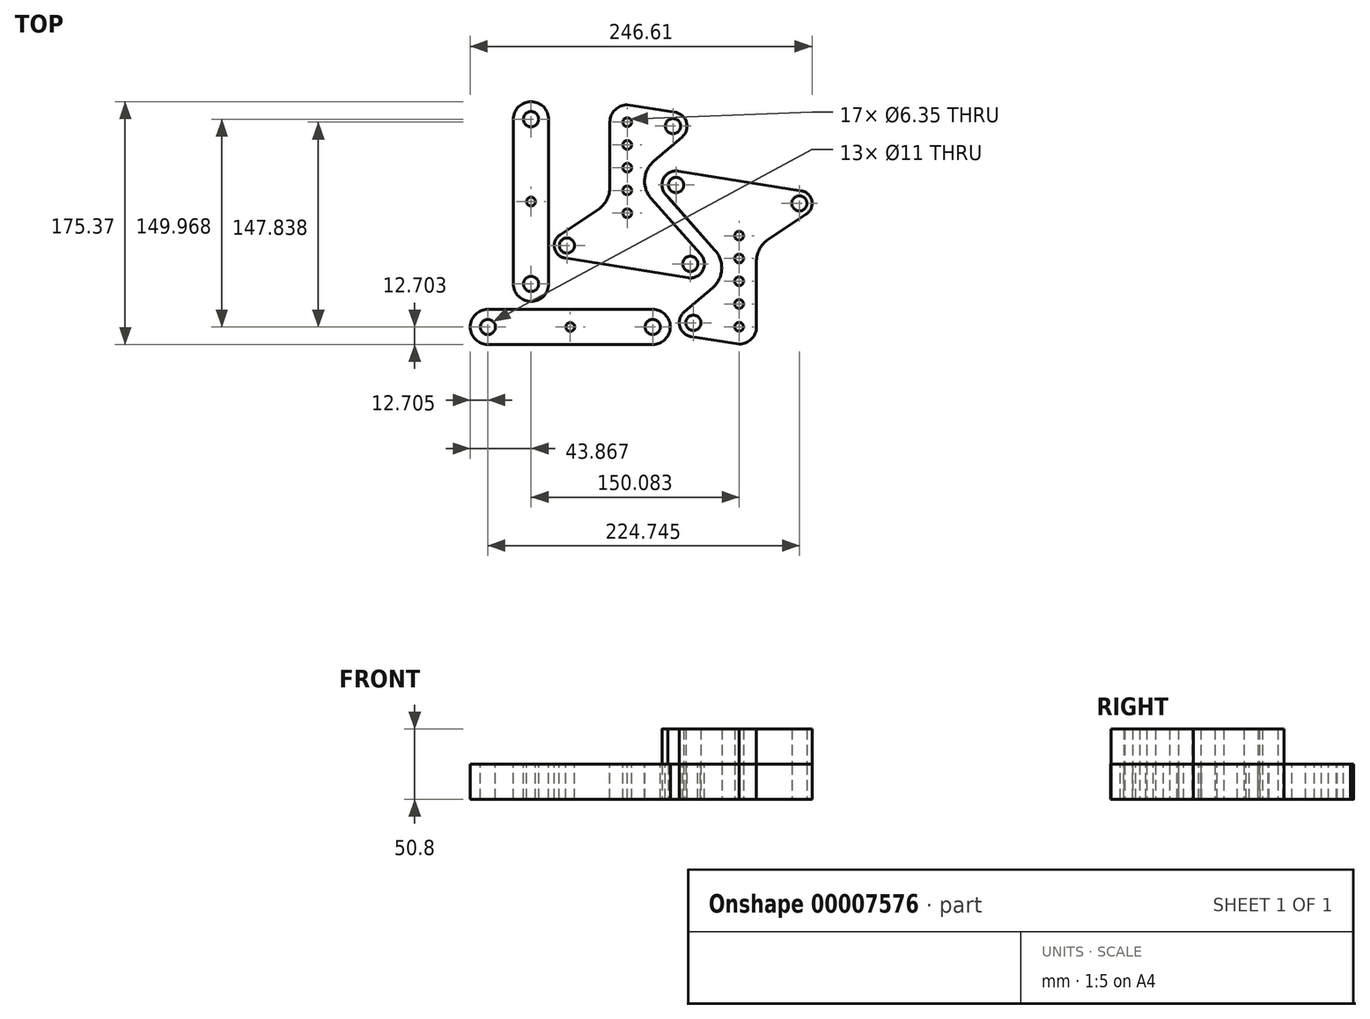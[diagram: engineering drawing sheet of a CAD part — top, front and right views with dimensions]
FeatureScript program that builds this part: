
annotation { "Feature Type Name" : "Feature", "Feature Type Description" : "" }
export const myFeature = defineFeature(function(context is Context, id is Id, definition is map)
    precondition{}
    {
        {
            var Q0;
            Q0=qCreatedBy(makeId("Top.planeOp"),FACE);
            var sketch = newSketch(context, id + "F0", { "sketchPlane" : qUnion([Q0])});
            skLineSegment(sketch, "E0", {"start": v(-216.15, 34.82) * mm, "end": v(113.5, 34.82) * mm});
            skLineSegment(sketch, "E1", {"start": v(-210.76, 13.28) * mm, "end": v(113.5, 13.28) * mm});
            skLineSegment(sketch, "E2", {"start": v(113.5, 0) * mm, "end": v(-200.85, 0) * mm});
            skLineSegment(sketch, "E3", {"start": v(-198.6, -86.18) * mm, "end": v(113.5, -86.18) * mm});
            skLineSegment(sketch, "E4", {"start": v(113.5, 34.82) * mm, "end": v(113.5, -86.18) * mm});
            skLineSegment(sketch, "E5", {"start": v(0, 62.68) * mm, "end": v(0, -125.74) * mm});
            skPoint(sketch, "E6", {"position": v(-45.5, 13.28) * mm});
            skPoint(sketch, "E7", {"position": v(43.5, 0) * mm});
            skPoint(sketch, "E8", {"position": v(-33, -86.18) * mm});
            skSolve(sketch);
        }
        {
            var Q0;
            Q0=qCreatedBy(makeId("Top.planeOp"),FACE);
            var sketch = newSketch(context, id + "F1", { "sketchPlane" : qUnion([Q0])});
            skLineSegment(sketch, "E9", {"start": v(113.5, 34.82) * mm, "end": v(113.5, -455.58) * mm});
            skLineSegment(sketch, "E10", {"start": v(113.5, 34.82) * mm, "end": v(-885.82, 34.82) * mm});
            skLineSegment(sketch, "E11", {"start": v(113.5, -7.25) * mm, "end": v(-888.28, -7.25) * mm});
            skLineSegment(sketch, "E12", {"start": v(113.5, -81.11) * mm, "end": v(-225.14, -81.11) * mm});
            skLineSegment(sketch, "E13", {"start": v(113.5, -46.44) * mm, "end": v(-202.6, -46.44) * mm});
            skLineSegment(sketch, "E14", {"start": v(113.5, -41.92) * mm, "end": v(-189.33, -41.92) * mm});
            skPoint(sketch, "E15", {"position": v(105.43, -46.44) * mm});
            skPoint(sketch, "E16", {"position": v(70.76, -7.25) * mm});
            skPoint(sketch, "E17", {"position": v(-31.57, -46.44) * mm});
            skPoint(sketch, "E18", {"position": v(31.57, -41.92) * mm});
            skPoint(sketch, "E19", {"position": v(-105.43, -41.92) * mm});
            skPoint(sketch, "E20", {"position": v(-66.24, -7.25) * mm});
            skPoint(sketch, "E21", {"position": v(66.24, -81.11) * mm});
            skPoint(sketch, "E22", {"position": v(-70.76, -81.11) * mm});
            skSolve(sketch);
        }
        {
            var Q0;
            Q0=qCreatedBy(makeId("Top.planeOp"),FACE);
            var sketch = newSketch(context, id + "F2", { "sketchPlane" : qUnion([Q0])});
            skCircle(sketch, "E23", {"center": v(-66.24, -7.25) * mm, "radius": 19.05 * mm});
            skCircle(sketch, "E24", {"center": v(-105.43, -41.92) * mm, "radius": 19.05 * mm});
            skCircle(sketch, "E25", {"center": v(-31.57, -46.44) * mm, "radius": 19.05 * mm});
            skCircle(sketch, "E26", {"center": v(-70.76, -81.11) * mm, "radius": 19.05 * mm});
            skCircle(sketch, "E27", {"center": v(70.76, -7.25) * mm, "radius": 19.05 * mm});
            skCircle(sketch, "E28", {"center": v(31.57, -41.92) * mm, "radius": 19.05 * mm});
            skCircle(sketch, "E29", {"center": v(105.43, -46.44) * mm, "radius": 19.05 * mm});
            skCircle(sketch, "E30", {"center": v(66.24, -81.11) * mm, "radius": 19.05 * mm});
            skCircle(sketch, "E31", {"center": v(43.5, 0) * mm, "radius": 9.16 * mm});
            skCircle(sketch, "E32", {"center": v(-45.5, 13.28) * mm, "radius": 10.13 * mm});
            skCircle(sketch, "E33", {"center": v(-45.5, 13.28) * mm, "radius": 5.5 * mm});
            skCircle(sketch, "E34", {"center": v(43.5, 0) * mm, "radius": 5.5 * mm});
            skCircle(sketch, "E35", {"center": v(-33, -86.18) * mm, "radius": 5.5 * mm});
            skCircle(sketch, "E36", {"center": v(-33, -86.18) * mm, "radius": 10.13 * mm});
            skLineSegment(sketch, "E37", {"start": v(-43.9, 23.28) * mm, "end": v(44.95, 9.04) * mm});
            skLineSegment(sketch, "E38", {"start": v(48.6, -7.61) * mm, "end": v(20.98, -26.09) * mm});
            skLineSegment(sketch, "E39", {"start": v(-53.08, 6.56) * mm, "end": v(-17.31, -33.8) * mm});
            skCircle(sketch, "E40", {"center": v(0, -89.06) * mm, "radius": 12.52 * mm});
            skLineSegment(sketch, "E41", {"start": v(-34.56, -96.2) * mm, "end": v(0, -101.58) * mm});
            skLineSegment(sketch, "E42", {"start": v(12.52, -89.06) * mm, "end": v(12.52, -42.2) * mm});
            skLineSegment(sketch, "E43", {"start": v(-39.61, -78.5) * mm, "end": v(-19.14, -60.88) * mm});
            skPoint(sketch, "E44", {"position": v(0, -23.32) * mm});
            skCircle(sketch, "E45", {"center": v(0, -23.32) * mm, "radius": 3.18 * mm});
            skCircle(sketch, "E46", {"center": v(0, -39.75) * mm, "radius": 3.18 * mm});
            skCircle(sketch, "E47", {"center": v(0, -56.19) * mm, "radius": 3.18 * mm});
            skCircle(sketch, "E48", {"center": v(0, -72.62) * mm, "radius": 3.18 * mm});
            skCircle(sketch, "E49", {"center": v(0, -89.06) * mm, "radius": 3.18 * mm});
            skLineSegment(sketch, "E50", {"start": v(0, -101.58) * mm, "end": v(0, 16.25) * mm});
            skSolve(sketch);
        }
        {
            var Q0;
            {var subQ13=sQuery(id+"F2.wireOp",EDGE,"E43");Q0=makeQuery(id+"F2.imprint","IMPRINT",FACE,{"disambiguationData":[TD([[makeQuery(id+"F2.imprint","IMPRINT",EDGE,{"derivedFrom":subQ13}),-1.0]])]});}
            var Q1;
            {var subQ18=sQuery(id+"F2.wireOp",EDGE,"E38");Q1=makeQuery(id+"F2.imprint","IMPRINT",FACE,{"disambiguationData":[TD([[makeQuery(id+"F2.imprint","IMPRINT",EDGE,{"derivedFrom":subQ18}),-1.0]])]});}
            var Q2;
            Q2=makeQuery(id+"F2.imprint","IMPRINT",FACE,{"disambiguationData":[TD([[makeQuery(id+"F2.imprint","IMPRINT",EDGE,{"derivedFrom":sQuery(id+"F2.wireOp",EDGE,"E33")}),-1.0]])]});
            var Q3;
            Q3=makeQuery(id+"F2.imprint","IMPRINT",FACE,{"disambiguationData":[TD([[makeQuery(id+"F2.imprint","IMPRINT",EDGE,{"derivedFrom":sQuery(id+"F2.wireOp",EDGE,"E34")}),-1.0]])]});
            var Q4;
            {var subQ3=sQuery(id+"F2.wireOp",EDGE,"E40");var subQ7=makeQuery(id+"F2.imprint","INTERSECT",VERTEX,{"derivedFrom":[subQ3,sQuery(id+"F2.wireOp",EDGE,"E42")]});Q4=makeQuery(id+"F2.imprint","IMPRINT",FACE,{"disambiguationData":[TD([[makeQuery(id+"F2.imprint","IMPRINT",EDGE,{"disambiguationData":[TD([[subQ7,-1.0]])],"derivedFrom":subQ3}),1.0]])]});}
            var Q5;
            {var subQ3=sQuery(id+"F2.wireOp",EDGE,"E40");var subQ6=sQuery(id+"F2.wireOp",EDGE,"E41");var subQ8=makeQuery(id+"F2.imprint","INTERSECT",VERTEX,{"derivedFrom":[subQ3,subQ6]});Q5=makeQuery(id+"F2.imprint","IMPRINT",FACE,{"disambiguationData":[TD([[makeQuery(id+"F2.imprint","IMPRINT",EDGE,{"disambiguationData":[TD([[subQ8,1.0]])],"derivedFrom":subQ3}),1.0]])]});}
            var Q6;
            Q6=makeQuery(id+"F2.imprint","IMPRINT",FACE,{"disambiguationData":[TD([[makeQuery(id+"F2.imprint","IMPRINT",EDGE,{"derivedFrom":sQuery(id+"F2.wireOp",EDGE,"E35")}),-1.0]])]});
            extrude(context, id + "F3", {"entities" : qUnion([Q0, Q1, Q2, Q3, Q4, Q5, Q6]), "depth" : 25.4 * mm});
        }
        {
            var Q0;
            Q0=makeQuery(id+"F3.opExtrude","CAP_FACE",FACE,{"disambiguationData":[OSD([sQuery(id+"F2.wireOp",EDGE,"E23"),sQuery(id+"F2.wireOp",EDGE,"E25"),sQuery(id+"F2.wireOp",EDGE,"E28"),sQuery(id+"F2.wireOp",EDGE,"E31"),sQuery(id+"F2.wireOp",EDGE,"E32"),sQuery(id+"F2.wireOp",EDGE,"E33"),sQuery(id+"F2.wireOp",EDGE,"E34"),sQuery(id+"F2.wireOp",EDGE,"E35"),sQuery(id+"F2.wireOp",EDGE,"E36"),sQuery(id+"F2.wireOp",EDGE,"E37"),sQuery(id+"F2.wireOp",EDGE,"E38"),sQuery(id+"F2.wireOp",EDGE,"E39"),sQuery(id+"F2.wireOp",EDGE,"E40"),sQuery(id+"F2.wireOp",EDGE,"E41"),sQuery(id+"F2.wireOp",EDGE,"E42"),sQuery(id+"F2.wireOp",EDGE,"E43"),sQuery(id+"F2.wireOp",EDGE,"E45"),sQuery(id+"F2.wireOp",EDGE,"E46"),sQuery(id+"F2.wireOp",EDGE,"E47"),sQuery(id+"F2.wireOp",EDGE,"E48"),sQuery(id+"F2.wireOp",EDGE,"E49")])],"isStart":false});
            var sketch = newSketch(context, id + "F4", { "sketchPlane" : qUnion([Q0])});
            skArc(sketch, "E51", {"start": v(-39.61, -78.5) * mm, "mid": v(-42.74, -88.96) * mm, "end": v(-34.56, -96.2) * mm});
            skArc(sketch, "E52", {"start": v(48.6, -7.61) * mm, "mid": v(52.45, 1.96) * mm, "end": v(44.95, 9.04) * mm});
            skArc(sketch, "E53", {"start": v(20.98, -26.09) * mm, "mid": v(14.7, -33.07) * mm, "end": v(12.52, -42.2) * mm});
            skArc(sketch, "E54", {"start": v(0, -101.58) * mm, "mid": v(8.85, -97.91) * mm, "end": v(12.52, -89.06) * mm});
            skArc(sketch, "E55", {"start": v(-19.14, -60.88) * mm, "mid": v(-12.56, -47.72) * mm, "end": v(-17.31, -33.8) * mm});
            skArc(sketch, "E56", {"start": v(-43.9, 23.28) * mm, "mid": v(-54.51, 17.91) * mm, "end": v(-52.7, 6.15) * mm});
            skLineSegment(sketch, "E57", {"start": v(-17.31, -33.8) * mm, "end": v(-52.7, 6.15) * mm});
            skLineSegment(sketch, "E58", {"start": v(-43.9, 23.28) * mm, "end": v(44.95, 9.04) * mm});
            skLineSegment(sketch, "E59", {"start": v(48.6, -7.61) * mm, "end": v(20.98, -26.09) * mm});
            skLineSegment(sketch, "E60", {"start": v(12.52, -42.2) * mm, "end": v(12.52, -89.06) * mm});
            skLineSegment(sketch, "E61", {"start": v(0, -101.58) * mm, "end": v(-34.56, -96.2) * mm});
            skLineSegment(sketch, "E62", {"start": v(-39.61, -78.5) * mm, "end": v(-19.14, -60.88) * mm});
            skCircle(sketch, "E63", {"center": v(-33, -86.18) * mm, "radius": 5.5 * mm});
            skCircle(sketch, "E64", {"center": v(0, -89.06) * mm, "radius": 3.18 * mm});
            skCircle(sketch, "E65", {"center": v(0, -72.62) * mm, "radius": 3.18 * mm});
            skCircle(sketch, "E66", {"center": v(-45.5, 13.28) * mm, "radius": 5.5 * mm});
            skCircle(sketch, "E67", {"center": v(43.5, 0) * mm, "radius": 5.5 * mm});
            skCircle(sketch, "E68", {"center": v(0, -56.19) * mm, "radius": 3.18 * mm});
            skCircle(sketch, "E69", {"center": v(0, -39.75) * mm, "radius": 3.18 * mm});
            skCircle(sketch, "E70", {"center": v(0, -23.32) * mm, "radius": 3.18 * mm});
            skLineSegment(sketch, "E71", {"start": v(-162.78, 60.77) * mm, "end": v(-162.78, -58.13) * mm});
            skLineSegment(sketch, "E72", {"start": v(-137.38, -58.13) * mm, "end": v(-137.38, 60.77) * mm});
            skArc(sketch, "E73", {"start": v(-137.38, 60.77) * mm, "mid": v(-150.08, 73.47) * mm, "end": v(-162.78, 60.77) * mm});
            skArc(sketch, "E74", {"start": v(-162.78, -58.13) * mm, "mid": v(-150.08, -70.83) * mm, "end": v(-137.38, -58.13) * mm});
            skCircle(sketch, "E75", {"center": v(-150.08, 60.77) * mm, "radius": 5.5 * mm});
            skCircle(sketch, "E76", {"center": v(-150.08, -58.13) * mm, "radius": 5.5 * mm});
            skCircle(sketch, "E77", {"center": v(-150.08, 1.32) * mm, "radius": 3.18 * mm});
            skPoint(sketch, "E77.centerSnap0", {"position": v(-121.63, -106.83) * mm});
            skArc(sketch, "E78", {"start": v(-41.09, 48.09) * mm, "mid": v(-37.96, 58.55) * mm, "end": v(-46.14, 65.78) * mm});
            skArc(sketch, "E79", {"start": v(-129.3, -22.8) * mm, "mid": v(-133.15, -32.37) * mm, "end": v(-125.65, -39.46) * mm});
            skArc(sketch, "E80", {"start": v(-101.68, -4.33) * mm, "mid": v(-95.4, 2.66) * mm, "end": v(-93.22, 11.8) * mm});
            skArc(sketch, "E81", {"start": v(-80.7, 71.16) * mm, "mid": v(-89.55, 67.5) * mm, "end": v(-93.22, 58.64) * mm});
            skArc(sketch, "E82", {"start": v(-61.56, 30.46) * mm, "mid": v(-68.14, 17.3) * mm, "end": v(-63.39, 3.4) * mm});
            skArc(sketch, "E83", {"start": v(-36.8, -53.7) * mm, "mid": v(-26.19, -48.33) * mm, "end": v(-28, -36.57) * mm});
            skLineSegment(sketch, "E84", {"start": v(-63.39, 3.4) * mm, "end": v(-28, -36.57) * mm});
            skLineSegment(sketch, "E85", {"start": v(-36.8, -53.7) * mm, "end": v(-125.65, -39.46) * mm});
            skLineSegment(sketch, "E86", {"start": v(-129.3, -22.8) * mm, "end": v(-101.68, -4.33) * mm});
            skLineSegment(sketch, "E87", {"start": v(-93.22, 11.8) * mm, "end": v(-93.22, 58.64) * mm});
            skLineSegment(sketch, "E88", {"start": v(-80.7, 71.16) * mm, "end": v(-46.14, 65.78) * mm});
            skLineSegment(sketch, "E89", {"start": v(-41.09, 48.09) * mm, "end": v(-61.56, 30.46) * mm});
            skCircle(sketch, "E90", {"center": v(-47.7, 55.77) * mm, "radius": 5.5 * mm});
            skCircle(sketch, "E91", {"center": v(-80.7, 58.64) * mm, "radius": 3.18 * mm});
            skCircle(sketch, "E92", {"center": v(-80.7, 42.2) * mm, "radius": 3.18 * mm});
            skCircle(sketch, "E93", {"center": v(-35.2, -43.7) * mm, "radius": 5.5 * mm});
            skCircle(sketch, "E94", {"center": v(-124.2, -30.41) * mm, "radius": 5.5 * mm});
            skCircle(sketch, "E95", {"center": v(-80.7, 25.77) * mm, "radius": 3.18 * mm});
            skCircle(sketch, "E96", {"center": v(-80.7, 9.34) * mm, "radius": 3.18 * mm});
            skCircle(sketch, "E97", {"center": v(-80.7, -7.1) * mm, "radius": 3.18 * mm});
            skLineSegment(sketch, "E98", {"start": v(-181.25, -101.9) * mm, "end": v(-62.35, -101.9) * mm});
            skLineSegment(sketch, "E99", {"start": v(-62.35, -76.5) * mm, "end": v(-181.25, -76.5) * mm});
            skArc(sketch, "E100", {"start": v(-181.25, -76.5) * mm, "mid": v(-193.95, -89.2) * mm, "end": v(-181.25, -101.9) * mm});
            skArc(sketch, "E101", {"start": v(-62.35, -101.9) * mm, "mid": v(-49.65, -89.2) * mm, "end": v(-62.35, -76.5) * mm});
            skCircle(sketch, "E102", {"center": v(-181.25, -89.2) * mm, "radius": 5.5 * mm});
            skCircle(sketch, "E103", {"center": v(-62.35, -89.2) * mm, "radius": 5.5 * mm});
            skCircle(sketch, "E104", {"center": v(-121.8, -89.2) * mm, "radius": 3.18 * mm});
            skPoint(sketch, "E104.centerSnap0", {"position": v(-121.8, -76.5) * mm});
            skArc(sketch, "E105", {"start": v(36.79, -33.88) * mm, "mid": v(33.66, -44.34) * mm, "end": v(41.84, -51.57) * mm});
            skArc(sketch, "E106", {"start": v(125, 37) * mm, "mid": v(128.85, 46.57) * mm, "end": v(121.35, 53.66) * mm});
            skArc(sketch, "E107", {"start": v(97.38, 18.53) * mm, "mid": v(91.1, 11.54) * mm, "end": v(88.92, 2.4) * mm});
            skArc(sketch, "E108", {"start": v(76.4, -56.96) * mm, "mid": v(85.25, -53.3) * mm, "end": v(88.92, -44.44) * mm});
            skArc(sketch, "E109", {"start": v(57.26, -16.26) * mm, "mid": v(63.84, -3.1) * mm, "end": v(59.09, 10.81) * mm});
            skArc(sketch, "E110", {"start": v(32.5, 67.9) * mm, "mid": v(21.89, 62.53) * mm, "end": v(23.7, 50.77) * mm});
            skLineSegment(sketch, "E111", {"start": v(59.09, 10.81) * mm, "end": v(23.7, 50.77) * mm});
            skLineSegment(sketch, "E112", {"start": v(32.5, 67.9) * mm, "end": v(121.35, 53.66) * mm});
            skLineSegment(sketch, "E113", {"start": v(125, 37) * mm, "end": v(97.38, 18.53) * mm});
            skLineSegment(sketch, "E114", {"start": v(88.92, 2.4) * mm, "end": v(88.92, -44.44) * mm});
            skLineSegment(sketch, "E115", {"start": v(76.4, -56.96) * mm, "end": v(41.84, -51.57) * mm});
            skLineSegment(sketch, "E116", {"start": v(36.79, -33.88) * mm, "end": v(57.26, -16.26) * mm});
            skCircle(sketch, "E117", {"center": v(43.4, -41.56) * mm, "radius": 5.5 * mm});
            skCircle(sketch, "E118", {"center": v(76.4, -44.44) * mm, "radius": 3.18 * mm});
            skCircle(sketch, "E119", {"center": v(76.4, -28) * mm, "radius": 3.18 * mm});
            skCircle(sketch, "E120", {"center": v(30.9, 57.9) * mm, "radius": 5.5 * mm});
            skCircle(sketch, "E121", {"center": v(119.9, 44.62) * mm, "radius": 5.5 * mm});
            skCircle(sketch, "E122", {"center": v(76.4, -11.57) * mm, "radius": 3.18 * mm});
            skCircle(sketch, "E123", {"center": v(76.4, 4.86) * mm, "radius": 3.18 * mm});
            skCircle(sketch, "E124", {"center": v(76.4, 21.3) * mm, "radius": 3.18 * mm});
            skSolve(sketch);
        }
        {
            var Q0;
            Q0=makeQuery(id+"F4.imprint","IMPRINT",FACE,{"disambiguationData":[TD([[makeQuery(id+"F4.imprint","IMPRINT",EDGE,{"derivedFrom":sQuery(id+"F4.wireOp",EDGE,"E51")}),1.0]])]});
            extrude(context, id + "F5", {"entities" : qUnion([Q0]), "depth" : 25.4 * mm});
        }
        {
            var Q0;
            Q0=makeQuery(id+"F4.imprint","IMPRINT",FACE,{"disambiguationData":[TD([[makeQuery(id+"F4.imprint","IMPRINT",EDGE,{"derivedFrom":sQuery(id+"F4.wireOp",EDGE,"E71")}),1.0]])]});
            var Q1;
            Q1=makeQuery(id+"F4.imprint","IMPRINT",FACE,{"disambiguationData":[TD([[makeQuery(id+"F4.imprint","IMPRINT",EDGE,{"derivedFrom":sQuery(id+"F4.wireOp",EDGE,"E98")}),1.0]])]});
            var Q2;
            Q2=makeQuery(id+"F4.imprint","IMPRINT",FACE,{"disambiguationData":[TD([[makeQuery(id+"F4.imprint","IMPRINT",EDGE,{"derivedFrom":sQuery(id+"F4.wireOp",EDGE,"E78")}),1.0]])]});
            extrude(context, id + "F6", {"entities" : qUnion([Q0, Q1, Q2]), "oppositeDirection" : true, "depth" : 25.4 * mm});
        }
    });
